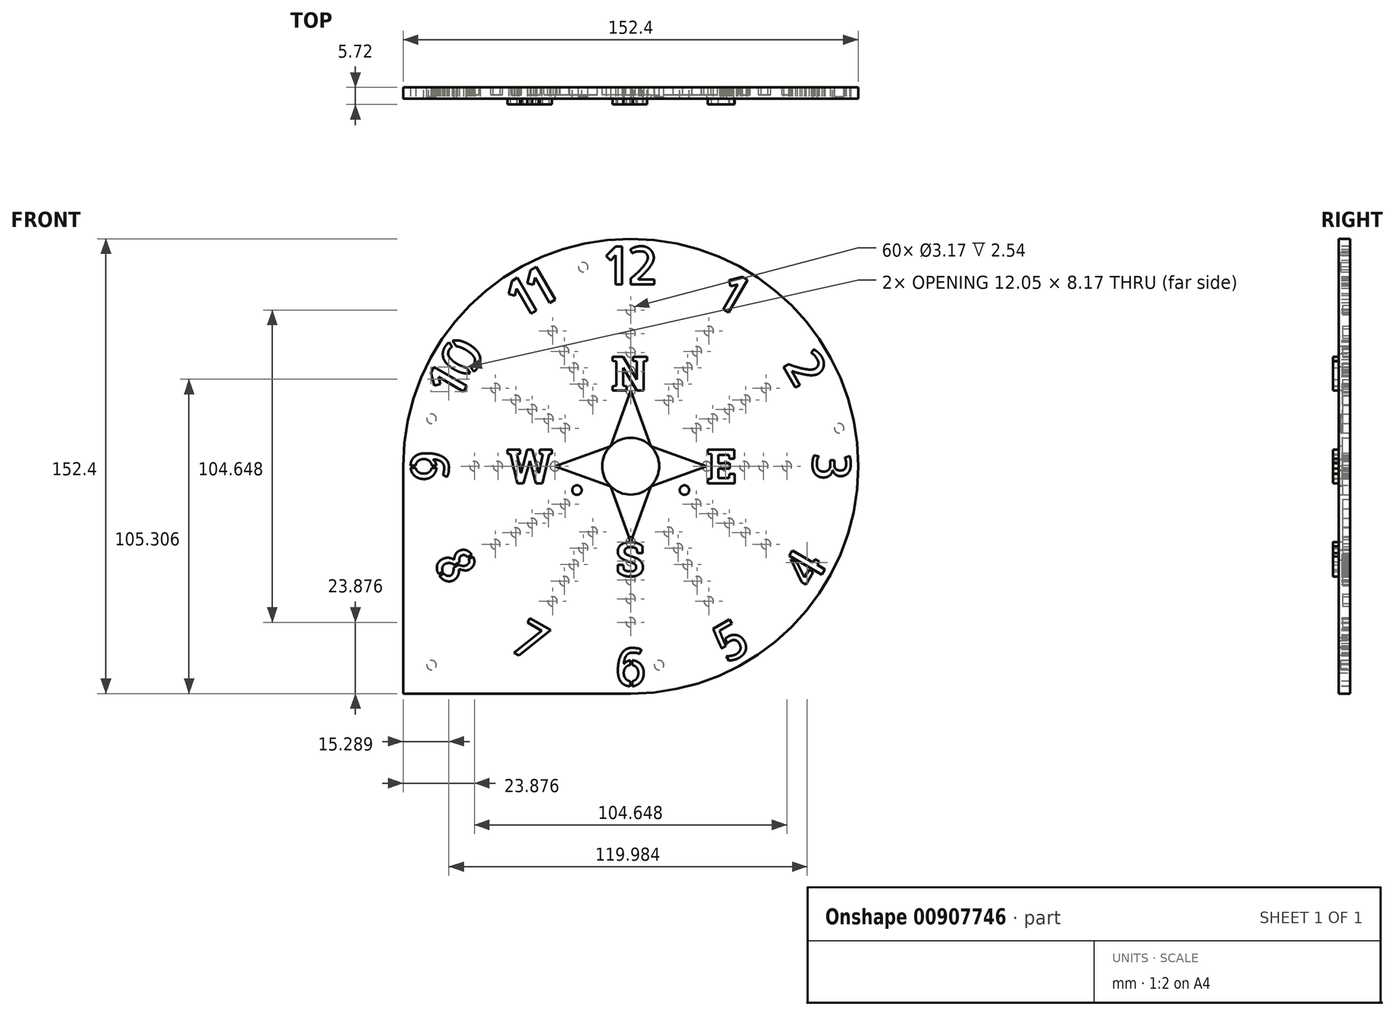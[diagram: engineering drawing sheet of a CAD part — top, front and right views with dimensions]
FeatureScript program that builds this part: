
annotation { "Feature Type Name" : "Feature", "Feature Type Description" : "" }
export const myFeature = defineFeature(function(context is Context, id is Id, definition is map)
    precondition{}
    {
        {
            var Q0;
            Q0=qCreatedBy(makeId("Front.planeOp"),FACE);
            var sketch = newSketch(context, id + "F0", { "sketchPlane" : qUnion([Q0])});
            skCircle(sketch, "E0", {"center": v(0, 0) * mm, "radius": 9.53 * mm});
            skCircle(sketch, "E1", {"center": v(-18, -8) * mm, "radius": 1.59 * mm});
            skCircle(sketch, "E2.1.0.0", {"center": v(18, -8) * mm, "radius": 1.59 * mm});
            skLineSegment(sketch, "E2.direction1", {"start": v(-18, -8) * mm, "end": v(18, -8) * mm, "construction": true});
            skArc(sketch, "E3", {"start": v(0, -76.2) * mm, "mid": v(53.88, 53.88) * mm, "end": v(-76.2, 0) * mm});
            skLineSegment(sketch, "E4", {"start": v(-76.2, 0) * mm, "end": v(-76.2, -76.2) * mm});
            skLineSegment(sketch, "E5", {"start": v(-76.2, -76.2) * mm, "end": v(0, -76.2) * mm});
            skSolve(sketch);
        }
        {
            var Q0;
            Q0 = qSketchRegion(id + "F0", true);
            extrude(context, id + "F1", {"entities" : qUnion([Q0]), "depth" : 3.8 * mm, "offsetDistance" : 25.4 * mm});
        }
        {
            var Q0;
            Q0=makeQuery(id+"F1.opExtrude","CAP_FACE",FACE,{"disambiguationData":[OSD([sQuery(id+"F0.wireOp",EDGE,"E0"),sQuery(id+"F0.wireOp",EDGE,"E1"),sQuery(id+"F0.wireOp",EDGE,"E2.1.0.0"),sQuery(id+"F0.wireOp",EDGE,"E3"),sQuery(id+"F0.wireOp",EDGE,"E4"),sQuery(id+"F0.wireOp",EDGE,"E5")])],"isStart":false});
            var sketch = newSketch(context, id + "F2", { "sketchPlane" : qUnion([Q0])});
            skLineSegment(sketch, "E6", {"start": v(0, 38.1) * mm, "end": v(-1.9, 57.15) * mm});
            skLineSegment(sketch, "E7", {"start": v(-1.9, 57.15) * mm, "end": v(1.9, 57.15) * mm});
            skLineSegment(sketch, "E8", {"start": v(1.9, 57.15) * mm, "end": v(0, 38.1) * mm});
            skLineSegment(sketch, "E9.1.0", {"start": v(-26.93, 50.45) * mm, "end": v(-19.05, 33) * mm});
            skLineSegment(sketch, "E9.1.1", {"start": v(-19.05, 33) * mm, "end": v(-30.22, 48.54) * mm});
            skLineSegment(sketch, "E9.1.2", {"start": v(-30.22, 48.54) * mm, "end": v(-26.93, 50.45) * mm});
            skLineSegment(sketch, "E9.2.0", {"start": v(-48.54, 30.22) * mm, "end": v(-33, 19.05) * mm});
            skLineSegment(sketch, "E9.2.1", {"start": v(-33, 19.05) * mm, "end": v(-50.45, 26.93) * mm});
            skLineSegment(sketch, "E9.2.2", {"start": v(-50.45, 26.93) * mm, "end": v(-48.54, 30.22) * mm});
            skLineSegment(sketch, "E9.3.0", {"start": v(-57.15, 1.9) * mm, "end": v(-38.1, 0) * mm});
            skLineSegment(sketch, "E9.3.1", {"start": v(-38.1, 0) * mm, "end": v(-57.15, -1.9) * mm});
            skLineSegment(sketch, "E9.3.2", {"start": v(-57.15, -1.9) * mm, "end": v(-57.15, 1.9) * mm});
            skLineSegment(sketch, "E9.4.0", {"start": v(-50.45, -26.93) * mm, "end": v(-33, -19.05) * mm});
            skLineSegment(sketch, "E9.4.1", {"start": v(-33, -19.05) * mm, "end": v(-48.54, -30.22) * mm});
            skLineSegment(sketch, "E9.4.2", {"start": v(-48.54, -30.22) * mm, "end": v(-50.45, -26.93) * mm});
            skLineSegment(sketch, "E9.5.0", {"start": v(-30.22, -48.54) * mm, "end": v(-19.05, -33) * mm});
            skLineSegment(sketch, "E9.5.1", {"start": v(-19.05, -33) * mm, "end": v(-26.93, -50.45) * mm});
            skLineSegment(sketch, "E9.5.2", {"start": v(-26.93, -50.45) * mm, "end": v(-30.22, -48.54) * mm});
            skLineSegment(sketch, "E9.6.0", {"start": v(-1.9, -57.15) * mm, "end": v(0, -38.1) * mm});
            skLineSegment(sketch, "E9.6.1", {"start": v(0, -38.1) * mm, "end": v(1.9, -57.15) * mm});
            skLineSegment(sketch, "E9.6.2", {"start": v(1.9, -57.15) * mm, "end": v(-1.9, -57.15) * mm});
            skLineSegment(sketch, "E9.7.0", {"start": v(26.93, -50.45) * mm, "end": v(19.05, -33) * mm});
            skLineSegment(sketch, "E9.7.1", {"start": v(19.05, -33) * mm, "end": v(30.22, -48.54) * mm});
            skLineSegment(sketch, "E9.7.2", {"start": v(30.22, -48.54) * mm, "end": v(26.93, -50.45) * mm});
            skLineSegment(sketch, "E9.8.0", {"start": v(48.54, -30.22) * mm, "end": v(33, -19.05) * mm});
            skLineSegment(sketch, "E9.8.1", {"start": v(33, -19.05) * mm, "end": v(50.45, -26.93) * mm});
            skLineSegment(sketch, "E9.8.2", {"start": v(50.45, -26.93) * mm, "end": v(48.54, -30.22) * mm});
            skLineSegment(sketch, "E9.9.0", {"start": v(57.15, -1.9) * mm, "end": v(38.1, 0) * mm});
            skLineSegment(sketch, "E9.9.1", {"start": v(38.1, 0) * mm, "end": v(57.15, 1.9) * mm});
            skLineSegment(sketch, "E9.9.2", {"start": v(57.15, 1.9) * mm, "end": v(57.15, -1.9) * mm});
            skLineSegment(sketch, "E9.10.0", {"start": v(50.45, 26.93) * mm, "end": v(33, 19.05) * mm});
            skLineSegment(sketch, "E9.10.1", {"start": v(33, 19.05) * mm, "end": v(48.54, 30.22) * mm});
            skLineSegment(sketch, "E9.10.2", {"start": v(48.54, 30.22) * mm, "end": v(50.45, 26.93) * mm});
            skLineSegment(sketch, "E9.11.0", {"start": v(30.22, 48.54) * mm, "end": v(19.05, 33) * mm});
            skLineSegment(sketch, "E9.11.1", {"start": v(19.05, 33) * mm, "end": v(26.93, 50.45) * mm});
            skLineSegment(sketch, "E9.11.2", {"start": v(26.93, 50.45) * mm, "end": v(30.22, 48.54) * mm});
            skPoint(sketch, "E9.center", {"position": v(0, 0) * mm});
            skSolve(sketch);
        }
        {
            var Q0;
            Q0 = qSketchRegion(id + "F2", true);
            extrude(context, id + "F3", {"entities" : qUnion([Q0]), "operationType" : NewBodyOperationType.ADD, "oppositeDirection" : true, "depth" : 1.27 * mm, "offsetDistance" : 25.4 * mm});
        }
        {
            var Q0;
            Q0=makeQuery(id+"F1.opExtrude","CAP_FACE",FACE,{"disambiguationData":[OSD([sQuery(id+"F0.wireOp",EDGE,"E0"),sQuery(id+"F0.wireOp",EDGE,"E1"),sQuery(id+"F0.wireOp",EDGE,"E2.1.0.0"),sQuery(id+"F0.wireOp",EDGE,"E3"),sQuery(id+"F0.wireOp",EDGE,"E4"),sQuery(id+"F0.wireOp",EDGE,"E5")])],"isStart":false});
            var sketch = newSketch(context, id + "F4", { "sketchPlane" : qUnion([Q0])});
            skText(sketch, "E10", { "text": "12", "fontName": "AllertaStencil-Regular.ttf"});
            skText(sketch, "E11", { "text": "1", "fontName": "AllertaStencil-Regular.ttf"});
            skText(sketch, "E12", { "text": "2", "fontName": "AllertaStencil-Regular.ttf"});
            skText(sketch, "E13", { "text": "3", "fontName": "AllertaStencil-Regular.ttf"});
            skText(sketch, "E14", { "text": "4", "fontName": "AllertaStencil-Regular.ttf"});
            skText(sketch, "E15", { "text": "5", "fontName": "AllertaStencil-Regular.ttf"});
            skText(sketch, "E16", { "text": "6", "fontName": "AllertaStencil-Regular.ttf"});
            skText(sketch, "E17", { "text": "7", "fontName": "AllertaStencil-Regular.ttf"});
            skText(sketch, "E18", { "text": "8", "fontName": "AllertaStencil-Regular.ttf"});
            skText(sketch, "E19", { "text": "9", "fontName": "AllertaStencil-Regular.ttf"});
            skText(sketch, "E20", { "text": "10", "fontName": "AllertaStencil-Regular.ttf"});
            skText(sketch, "E21", { "text": "11", "fontName": "AllertaStencil-Regular.ttf"});
            const initialGuessF4  = {"E10": [-0.00874, 0.06096, 1, 0, 0.0127], "E11": [0.02774, 0.05437, 0.86603, -0.5, 0.0127], "E12": [0.05049, 0.03447, 0.5, -0.86603, 0.0127], "E13": [0.06096, 0.00497, 0, -1, 0.0127], "E14": [0.06097, -0.04172, 0.5, 0.86603, 0.0127], "E15": [0.03209, -0.06653, 0.86603, 0.5, 0.0127], "E16": [-0.00554, -0.07366, 1, 0, 0.0127], "E17": [-0.041, -0.06139, 0.86603, -0.5, 0.0127], "E18": [-0.06669, -0.03181, 0.5, -0.86603, 0.0127], "E19": [-0.06096, -0.00552, 0, 1, 0.0127], "E20": [-0.0578, 0.0218, 0.5, 0.86603, 0.0127], "E21": [-0.03662, 0.04925, 0.86603, 0.5, 0.0127]};
            skSetInitialGuess(sketch, initialGuessF4);
            skSolve(sketch);
        }
        {
            var Q0;
            Q0 = qSketchRegion(id + "F4", true);
            extrude(context, id + "F5", {"entities" : qUnion([Q0]), "operationType" : NewBodyOperationType.REMOVE, "oppositeDirection" : true, "depth" : 25.4 * mm, "offsetDistance" : 25.4 * mm});
        }
        {
            var Q0;
            Q0=makeQuery(id+"F1.opExtrude","CAP_FACE",FACE,{"disambiguationData":[OSD([sQuery(id+"F0.wireOp",EDGE,"E0"),sQuery(id+"F0.wireOp",EDGE,"E1"),sQuery(id+"F0.wireOp",EDGE,"E2.1.0.0"),sQuery(id+"F0.wireOp",EDGE,"E3"),sQuery(id+"F0.wireOp",EDGE,"E4"),sQuery(id+"F0.wireOp",EDGE,"E5")])],"isStart":false});
            var sketch = newSketch(context, id + "F6", { "sketchPlane" : qUnion([Q0])});
            skLineSegment(sketch, "E22", {"start": v(0, 25.4) * mm, "end": v(-6.74, 6.74) * mm});
            skLineSegment(sketch, "E23", {"start": v(-6.74, 6.74) * mm, "end": v(-25.4, 0) * mm});
            skLineSegment(sketch, "E24", {"start": v(-25.4, 0) * mm, "end": v(-6.74, -6.74) * mm});
            skLineSegment(sketch, "E25", {"start": v(-6.74, -6.74) * mm, "end": v(0, -25.4) * mm});
            skLineSegment(sketch, "E26", {"start": v(0, -25.4) * mm, "end": v(6.74, -6.74) * mm});
            skLineSegment(sketch, "E27", {"start": v(6.74, -6.74) * mm, "end": v(25.4, 0) * mm});
            skLineSegment(sketch, "E28", {"start": v(25.4, 0) * mm, "end": v(6.74, 6.74) * mm});
            skLineSegment(sketch, "E29", {"start": v(6.74, 6.74) * mm, "end": v(0, 25.4) * mm});
            skLineSegment(sketch, "E30", {"start": v(-6.74, 6.74) * mm, "end": v(0, 0) * mm, "construction": true});
            skLineSegment(sketch, "E31", {"start": v(0, 0) * mm, "end": v(6.74, 6.74) * mm, "construction": true});
            skLineSegment(sketch, "E32", {"start": v(0, 0) * mm, "end": v(-6.74, -6.74) * mm, "construction": true});
            skLineSegment(sketch, "E33", {"start": v(6.74, -6.74) * mm, "end": v(0, 0) * mm, "construction": true});
            skSolve(sketch);
        }
        {
            var Q0;
            Q0 = qSketchRegion(id + "F6", true);
            extrude(context, id + "F7", {"entities" : qUnion([Q0]), "operationType" : NewBodyOperationType.REMOVE, "oppositeDirection" : true, "depth" : 1.27 * mm, "offsetDistance" : 25.4 * mm});
        }
        {
            var Q0;
            Q0=makeQuery(id+"F1.opExtrude","CAP_FACE",FACE,{"disambiguationData":[OSD([sQuery(id+"F0.wireOp",EDGE,"E0"),sQuery(id+"F0.wireOp",EDGE,"E1"),sQuery(id+"F0.wireOp",EDGE,"E2.1.0.0"),sQuery(id+"F0.wireOp",EDGE,"E3"),sQuery(id+"F0.wireOp",EDGE,"E4"),sQuery(id+"F0.wireOp",EDGE,"E5")])],"isStart":false});
            var sketch = newSketch(context, id + "F8", { "sketchPlane" : qUnion([Q0])});
            skText(sketch, "E34", { "text": "N", "fontName": "RobotoSlab-Bold.ttf"});
            skText(sketch, "E35", { "text": "E", "fontName": "RobotoSlab-Bold.ttf"});
            skText(sketch, "E36", { "text": "W", "fontName": "RobotoSlab-Bold.ttf"});
            skText(sketch, "E37", { "text": "S\n", "fontName": "RobotoSlab-Bold.ttf"});
            const initialGuessF8  = {"E34": [-0.00647, 0.0254, 1, 0, 0.01143], "E35": [0.0254, -0.00571, 1, 0, 0.01143], "E36": [-0.04143, -0.00572, 1, 0, 0.01143], "E37": [-0.00507, -0.03683, 1, 0, 0.01143]};
            skSetInitialGuess(sketch, initialGuessF8);
            skSolve(sketch);
        }
        {
            var Q0;
            Q0 = qSketchRegion(id + "F8", true);
            extrude(context, id + "F9", {"entities" : qUnion([Q0]), "operationType" : NewBodyOperationType.ADD, "depth" : 1.9 * mm, "offsetDistance" : 25.4 * mm});
        }
        {
            var Q0;
            Q0=makeQuery(id+"F1.opExtrude","CAP_FACE",FACE,{"disambiguationData":[OSD([sQuery(id+"F0.wireOp",EDGE,"E0"),sQuery(id+"F0.wireOp",EDGE,"E1"),sQuery(id+"F0.wireOp",EDGE,"E2.1.0.0"),sQuery(id+"F0.wireOp",EDGE,"E3"),sQuery(id+"F0.wireOp",EDGE,"E4"),sQuery(id+"F0.wireOp",EDGE,"E5")])],"isStart":true});
            var sketch = newSketch(context, id + "F10", { "sketchPlane" : qUnion([Q0])});
            skCircle(sketch, "E38", {"center": v(-38.1, 0) * mm, "radius": 1.59 * mm});
            skCircle(sketch, "E39", {"center": v(-31.75, 0) * mm, "radius": 1.59 * mm});
            skCircle(sketch, "E40", {"center": v(-44.45, 0) * mm, "radius": 1.59 * mm});
            skCircle(sketch, "E41", {"center": v(-52.32, 0) * mm, "radius": 1.59 * mm});
            skCircle(sketch, "E42", {"center": v(-25.4, 0) * mm, "radius": 1.59 * mm});
            skCircle(sketch, "E43.1.0", {"center": v(-38.5, -22.23) * mm, "radius": 1.59 * mm});
            skCircle(sketch, "E43.1.1", {"center": v(-45.31, -26.16) * mm, "radius": 1.59 * mm});
            skCircle(sketch, "E43.1.2", {"center": v(-33, -19.05) * mm, "radius": 1.59 * mm});
            skCircle(sketch, "E43.1.3", {"center": v(-22, -12.7) * mm, "radius": 1.59 * mm});
            skCircle(sketch, "E43.1.4", {"center": v(-27.5, -15.87) * mm, "radius": 1.59 * mm});
            skCircle(sketch, "E43.2.0", {"center": v(-22.23, -38.5) * mm, "radius": 1.59 * mm});
            skCircle(sketch, "E43.2.1", {"center": v(-26.16, -45.31) * mm, "radius": 1.59 * mm});
            skCircle(sketch, "E43.2.2", {"center": v(-19.05, -33) * mm, "radius": 1.59 * mm});
            skCircle(sketch, "E43.2.3", {"center": v(-12.7, -22) * mm, "radius": 1.59 * mm});
            skCircle(sketch, "E43.2.4", {"center": v(-15.88, -27.5) * mm, "radius": 1.59 * mm});
            skCircle(sketch, "E43.3.0", {"center": v(0, -44.45) * mm, "radius": 1.59 * mm});
            skCircle(sketch, "E43.3.1", {"center": v(0, -52.32) * mm, "radius": 1.59 * mm});
            skCircle(sketch, "E43.3.2", {"center": v(0, -38.1) * mm, "radius": 1.59 * mm});
            skCircle(sketch, "E43.3.3", {"center": v(0, -25.4) * mm, "radius": 1.59 * mm});
            skCircle(sketch, "E43.3.4", {"center": v(0, -31.75) * mm, "radius": 1.59 * mm});
            skCircle(sketch, "E43.4.0", {"center": v(22.22, -38.5) * mm, "radius": 1.59 * mm});
            skCircle(sketch, "E43.4.1", {"center": v(26.16, -45.31) * mm, "radius": 1.59 * mm});
            skCircle(sketch, "E43.4.2", {"center": v(19.05, -33) * mm, "radius": 1.59 * mm});
            skCircle(sketch, "E43.4.3", {"center": v(12.7, -22) * mm, "radius": 1.59 * mm});
            skCircle(sketch, "E43.4.4", {"center": v(15.87, -27.5) * mm, "radius": 1.59 * mm});
            skCircle(sketch, "E43.5.0", {"center": v(38.5, -22.22) * mm, "radius": 1.59 * mm});
            skCircle(sketch, "E43.5.1", {"center": v(45.31, -26.16) * mm, "radius": 1.59 * mm});
            skCircle(sketch, "E43.5.2", {"center": v(33, -19.05) * mm, "radius": 1.59 * mm});
            skCircle(sketch, "E43.5.3", {"center": v(22, -12.7) * mm, "radius": 1.59 * mm});
            skCircle(sketch, "E43.5.4", {"center": v(27.5, -15.87) * mm, "radius": 1.59 * mm});
            skCircle(sketch, "E43.6.0", {"center": v(44.45, 0) * mm, "radius": 1.59 * mm});
            skCircle(sketch, "E43.6.1", {"center": v(52.32, 0) * mm, "radius": 1.59 * mm});
            skCircle(sketch, "E43.6.2", {"center": v(38.1, 0) * mm, "radius": 1.59 * mm});
            skCircle(sketch, "E43.6.3", {"center": v(25.4, 0) * mm, "radius": 1.59 * mm});
            skCircle(sketch, "E43.6.4", {"center": v(31.75, 0) * mm, "radius": 1.59 * mm});
            skCircle(sketch, "E43.7.0", {"center": v(38.5, 22.22) * mm, "radius": 1.59 * mm});
            skCircle(sketch, "E43.7.1", {"center": v(45.31, 26.16) * mm, "radius": 1.59 * mm});
            skCircle(sketch, "E43.7.2", {"center": v(33, 19.05) * mm, "radius": 1.59 * mm});
            skCircle(sketch, "E43.7.3", {"center": v(22, 12.7) * mm, "radius": 1.59 * mm});
            skCircle(sketch, "E43.7.4", {"center": v(27.5, 15.87) * mm, "radius": 1.59 * mm});
            skCircle(sketch, "E43.8.0", {"center": v(22.23, 38.5) * mm, "radius": 1.59 * mm});
            skCircle(sketch, "E43.8.1", {"center": v(26.16, 45.31) * mm, "radius": 1.59 * mm});
            skCircle(sketch, "E43.8.2", {"center": v(19.05, 33) * mm, "radius": 1.59 * mm});
            skCircle(sketch, "E43.8.3", {"center": v(12.7, 22) * mm, "radius": 1.59 * mm});
            skCircle(sketch, "E43.8.4", {"center": v(15.88, 27.5) * mm, "radius": 1.59 * mm});
            skCircle(sketch, "E43.9.0", {"center": v(0, 44.45) * mm, "radius": 1.59 * mm});
            skCircle(sketch, "E43.9.1", {"center": v(0, 52.32) * mm, "radius": 1.59 * mm});
            skCircle(sketch, "E43.9.2", {"center": v(0, 38.1) * mm, "radius": 1.59 * mm});
            skCircle(sketch, "E43.9.3", {"center": v(0, 25.4) * mm, "radius": 1.59 * mm});
            skCircle(sketch, "E43.9.4", {"center": v(0, 31.75) * mm, "radius": 1.59 * mm});
            skCircle(sketch, "E43.10.0", {"center": v(-22.23, 38.5) * mm, "radius": 1.59 * mm});
            skCircle(sketch, "E43.10.1", {"center": v(-26.16, 45.31) * mm, "radius": 1.59 * mm});
            skCircle(sketch, "E43.10.2", {"center": v(-19.05, 33) * mm, "radius": 1.59 * mm});
            skCircle(sketch, "E43.10.3", {"center": v(-12.7, 22) * mm, "radius": 1.59 * mm});
            skCircle(sketch, "E43.10.4", {"center": v(-15.88, 27.5) * mm, "radius": 1.59 * mm});
            skCircle(sketch, "E43.11.0", {"center": v(-38.5, 22.23) * mm, "radius": 1.59 * mm});
            skCircle(sketch, "E43.11.1", {"center": v(-45.31, 26.16) * mm, "radius": 1.59 * mm});
            skCircle(sketch, "E43.11.2", {"center": v(-33, 19.05) * mm, "radius": 1.59 * mm});
            skCircle(sketch, "E43.11.3", {"center": v(-22, 12.7) * mm, "radius": 1.59 * mm});
            skCircle(sketch, "E43.11.4", {"center": v(-27.5, 15.88) * mm, "radius": 1.59 * mm});
            skPoint(sketch, "E43.center", {"position": v(0, 0) * mm});
            skSolve(sketch);
        }
        {
            var Q0;
            Q0 = qSketchRegion(id + "F10", true);
            extrude(context, id + "F11", {"entities" : qUnion([Q0]), "operationType" : NewBodyOperationType.REMOVE, "oppositeDirection" : true, "depth" : 2.54 * mm, "offsetDistance" : 25.4 * mm});
        }
        {
            var Q0;
            Q0=makeQuery(id+"F1.opExtrude","CAP_FACE",FACE,{"disambiguationData":[OSD([sQuery(id+"F0.wireOp",EDGE,"E0"),sQuery(id+"F0.wireOp",EDGE,"E1"),sQuery(id+"F0.wireOp",EDGE,"E2.1.0.0"),sQuery(id+"F0.wireOp",EDGE,"E3"),sQuery(id+"F0.wireOp",EDGE,"E4"),sQuery(id+"F0.wireOp",EDGE,"E5")])],"isStart":true});
            var sketch = newSketch(context, id + "F12", { "sketchPlane" : qUnion([Q0])});
            skCircle(sketch, "E44", {"center": v(66.67, -66.67) * mm, "radius": 1.59 * mm});
            skCircle(sketch, "E45", {"center": v(-9.53, -66.67) * mm, "radius": 1.59 * mm});
            skCircle(sketch, "E46", {"center": v(-69.85, 12.7) * mm, "radius": 1.59 * mm});
            skCircle(sketch, "E47", {"center": v(15.87, 66.68) * mm, "radius": 1.59 * mm});
            skCircle(sketch, "E48", {"center": v(66.67, 15.88) * mm, "radius": 1.59 * mm});
            skSolve(sketch);
        }
        {
            var Q0;
            Q0 = qSketchRegion(id + "F12", true);
            extrude(context, id + "F13", {"entities" : qUnion([Q0]), "operationType" : NewBodyOperationType.REMOVE, "oppositeDirection" : true, "depth" : 3.17 * mm, "offsetDistance" : 25.4 * mm});
        }
    });
